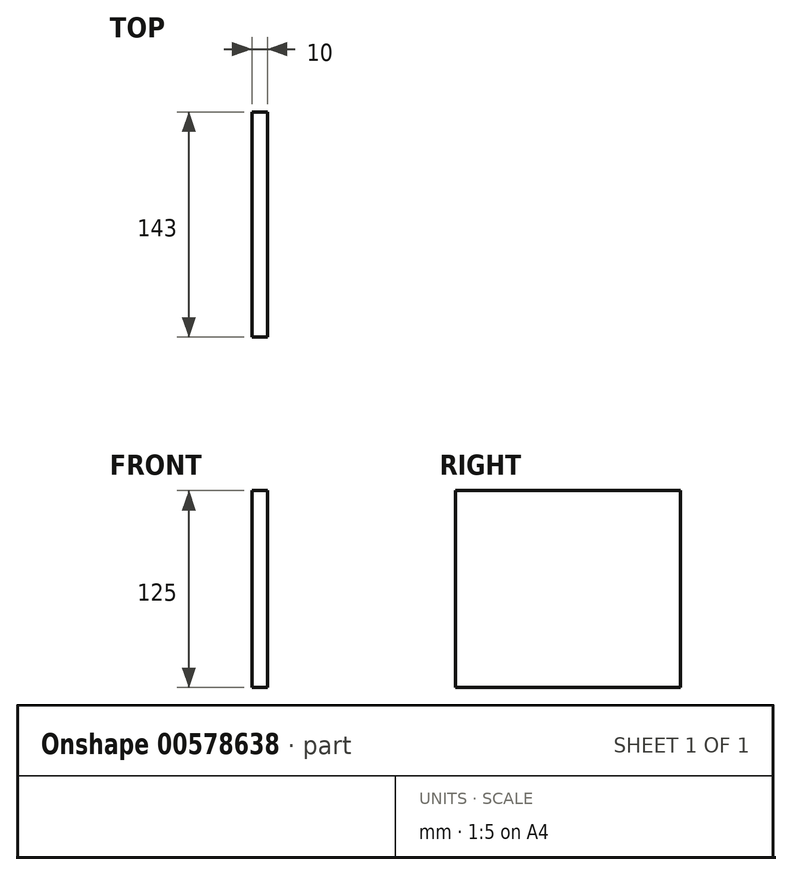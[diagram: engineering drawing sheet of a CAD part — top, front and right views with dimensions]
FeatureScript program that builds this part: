
annotation { "Feature Type Name" : "Feature", "Feature Type Description" : "" }
export const myFeature = defineFeature(function(context is Context, id is Id, definition is map)
    precondition{}
    {
        {
            var Q0;
            Q0=qCreatedBy(makeId("Right.planeOp"),FACE);
            var sketch = newSketch(context, id + "F0", { "sketchPlane" : qUnion([Q0])});
            skLineSegment(sketch, "E0.bottom", {"start": v(0, 0) * mm, "end": v(143, 0) * mm});
            skLineSegment(sketch, "E0.top", {"start": v(0, -125) * mm, "end": v(143, -125) * mm});
            skLineSegment(sketch, "E0.left", {"start": v(0, 0) * mm, "end": v(0, -125) * mm});
            skLineSegment(sketch, "E0.right", {"start": v(143, 0) * mm, "end": v(143, -125) * mm});
            skSolve(sketch);
        }
        {
            var Q0;
            Q0 = qSketchRegion(id + "F0", true);
            extrude(context, id + "F1", {"entities" : qUnion([Q0]), "depth" : 10 * mm, "offsetDistance" : 25 * mm});
        }
    });
